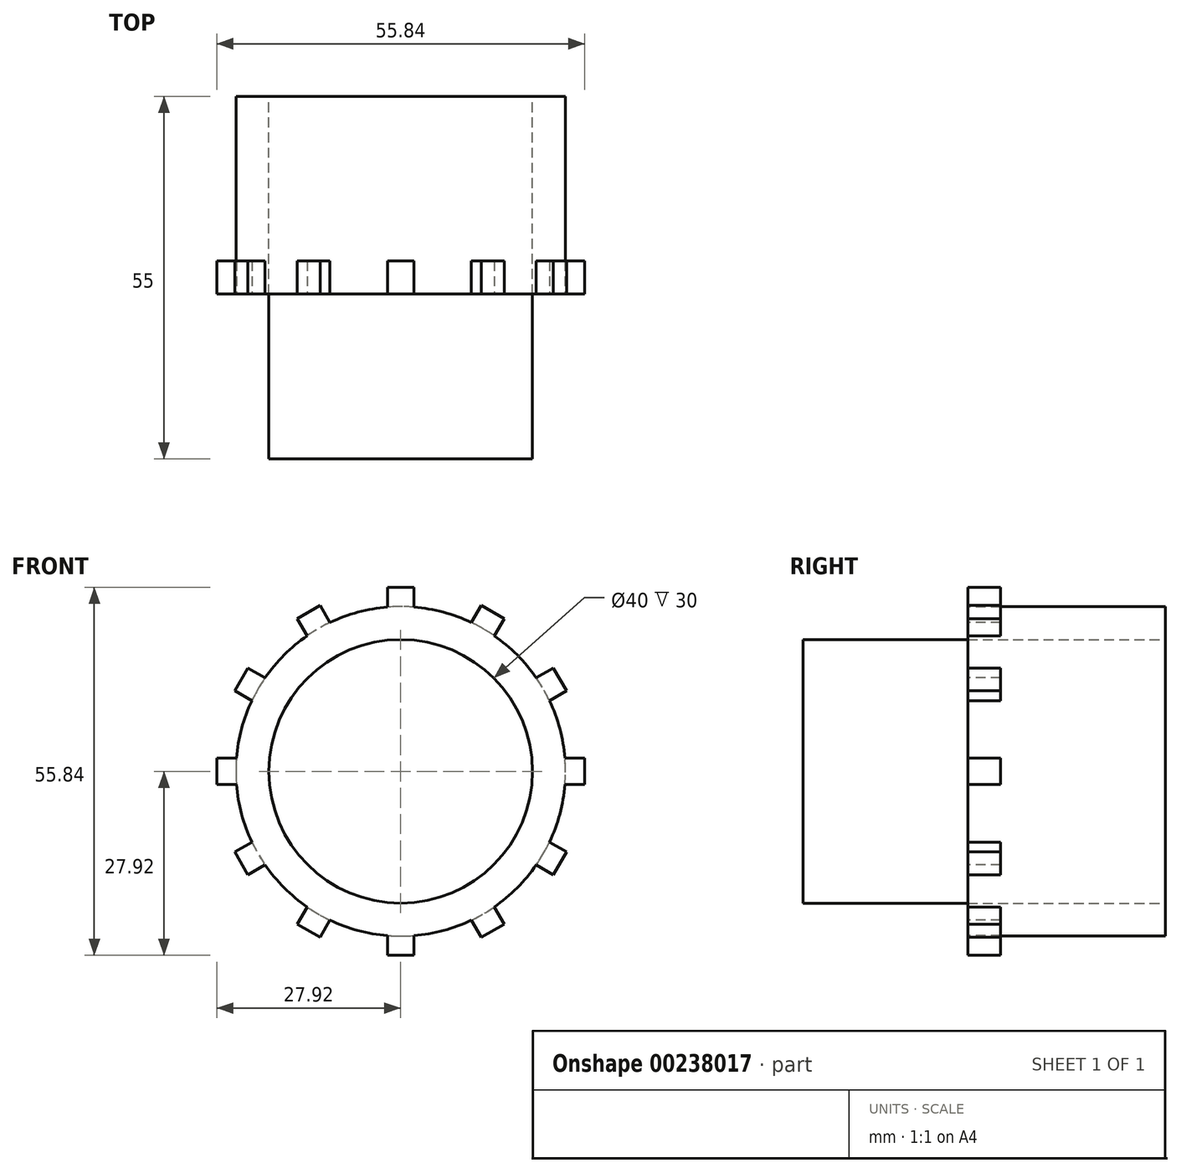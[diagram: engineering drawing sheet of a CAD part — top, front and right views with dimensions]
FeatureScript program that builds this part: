
annotation { "Feature Type Name" : "Feature", "Feature Type Description" : "" }
export const myFeature = defineFeature(function(context is Context, id is Id, definition is map)
    precondition{}
    {
        {
            var Q0;
            Q0=qCreatedBy(makeId("Front.planeOp"),FACE);
            var sketch = newSketch(context, id + "F0", { "sketchPlane" : qUnion([Q0])});
            skCircle(sketch, "E0", {"center": v(0, 0) * mm, "radius": 25 * mm});
            skCircle(sketch, "E1", {"center": v(0, 0) * mm, "radius": 20 * mm});
            skSolve(sketch);
        }
        {
            var Q0;
            Q0=makeQuery(id+"F0.imprint","IMPRINT",FACE,{"disambiguationData":[TD([[makeQuery(id+"F0.imprint","IMPRINT",EDGE,{"derivedFrom":sQuery(id+"F0.wireOp",EDGE,"E0")}),1.0]])]});
            extrude(context, id + "F1", {"entities" : qUnion([Q0]), "depth" : 30 * mm});
        }
        {
            var Q0;
            Q0=makeQuery(id+"F1.opExtrude","CAP_FACE",FACE,{"disambiguationData":[OSD([sQuery(id+"F0.wireOp",EDGE,"E0"),sQuery(id+"F0.wireOp",EDGE,"E1")])],"isStart":false});
            var sketch = newSketch(context, id + "F2", { "sketchPlane" : qUnion([Q0])});
            skArc(sketch, "E2.0", {"start": v(2, 24.92) * mm, "mid": v(0, 25) * mm, "end": v(-2, 24.92) * mm});
            skLineSegment(sketch, "E3", {"start": v(-2, 24.92) * mm, "end": v(-2, 27.92) * mm});
            skLineSegment(sketch, "E4", {"start": v(-2, 27.92) * mm, "end": v(2, 27.92) * mm});
            skLineSegment(sketch, "E5", {"start": v(2, 27.92) * mm, "end": v(2, 24.92) * mm});
            skSolve(sketch);
        }
        {
            var Q0;
            Q0=makeQuery(id+"F2.imprint","IMPRINT",FACE,{"disambiguationData":[TD([[makeQuery(id+"F2.imprint","IMPRINT",EDGE,{"derivedFrom":sQuery(id+"F2.wireOp",EDGE,"E2.0")}),-1.0]])]});
            extrude(context, id + "F3", {"entities" : qUnion([Q0]), "oppositeDirection" : true, "depth" : 5 * mm});
        }
        {
            var Q0;
            Q0=makeQuery(id+"F3.opExtrude","SWEPT_BODY",BODY,{"disambiguationData":[OSD([sQuery(id+"F2.wireOp",EDGE,"E2.0"),sQuery(id+"F2.wireOp",EDGE,"E3"),sQuery(id+"F2.wireOp",EDGE,"E4"),sQuery(id+"F2.wireOp",EDGE,"E5")])]});
            var Q1;
            Q1=makeQuery(id+"F1.opExtrude","SWEPT_FACE",FACE,{"disambiguationData":[OSD([sQuery(id+"F0.wireOp",EDGE,"E1")])]});
            circularPattern(context, id + "F4", {"operationType" : NewBodyOperationType.ADD, "entities" : qUnion([Q0]), "axis" : qUnion([Q1]), "angle" : 360 * degree, "instanceCount" : 12, "equalSpace" : true});
        }
        {
            var Q0;
            {var subQ0=makeQuery(id+"F3.opExtrude","CAP_FACE",FACE,{"disambiguationData":[OSD([sQuery(id+"F2.wireOp",EDGE,"E2.0"),sQuery(id+"F2.wireOp",EDGE,"E3"),sQuery(id+"F2.wireOp",EDGE,"E4"),sQuery(id+"F2.wireOp",EDGE,"E5")])],"isStart":true});Q0=makeQuery(id+"F4.boolean.opBoolean","MERGE",FACE,{"derivedFrom":[makeQuery(id+"F1.opExtrude","CAP_FACE",FACE,{"disambiguationData":[OSD([sQuery(id+"F0.wireOp",EDGE,"E0"),sQuery(id+"F0.wireOp",EDGE,"E1")])],"isStart":false}),subQ0,makeQuery(id+"F4.opPattern","COPY",FACE,{"derivedFrom":subQ0,"instanceName":"1"}),makeQuery(id+"F4.opPattern","COPY",FACE,{"derivedFrom":subQ0,"instanceName":"2"}),makeQuery(id+"F4.opPattern","COPY",FACE,{"derivedFrom":subQ0,"instanceName":"3"}),makeQuery(id+"F4.opPattern","COPY",FACE,{"derivedFrom":subQ0,"instanceName":"4"}),makeQuery(id+"F4.opPattern","COPY",FACE,{"derivedFrom":subQ0,"instanceName":"5"}),makeQuery(id+"F4.opPattern","COPY",FACE,{"derivedFrom":subQ0,"instanceName":"6"}),makeQuery(id+"F4.opPattern","COPY",FACE,{"derivedFrom":subQ0,"instanceName":"7"}),makeQuery(id+"F4.opPattern","COPY",FACE,{"derivedFrom":subQ0,"instanceName":"8"}),makeQuery(id+"F4.opPattern","COPY",FACE,{"derivedFrom":subQ0,"instanceName":"9"}),makeQuery(id+"F4.opPattern","COPY",FACE,{"derivedFrom":subQ0,"instanceName":"10"}),makeQuery(id+"F4.opPattern","COPY",FACE,{"derivedFrom":subQ0,"instanceName":"11"})]});}
            var sketch = newSketch(context, id + "F5", { "sketchPlane" : qUnion([Q0])});
            skCircle(sketch, "E6", {"center": v(0, 0) * mm, "radius": 20 * mm});
            skSolve(sketch);
        }
        {
            var Q0;
            Q0=makeQuery(id+"F5.imprint","IMPRINT",FACE,{"disambiguationData":[TD([[makeQuery(id+"F5.imprint","IMPRINT",EDGE,{"derivedFrom":sQuery(id+"F5.wireOp",EDGE,"E6")}),1.0]])]});
            extrude(context, id + "F6", {"entities" : qUnion([Q0]), "depth" : 25 * mm});
        }
    });
